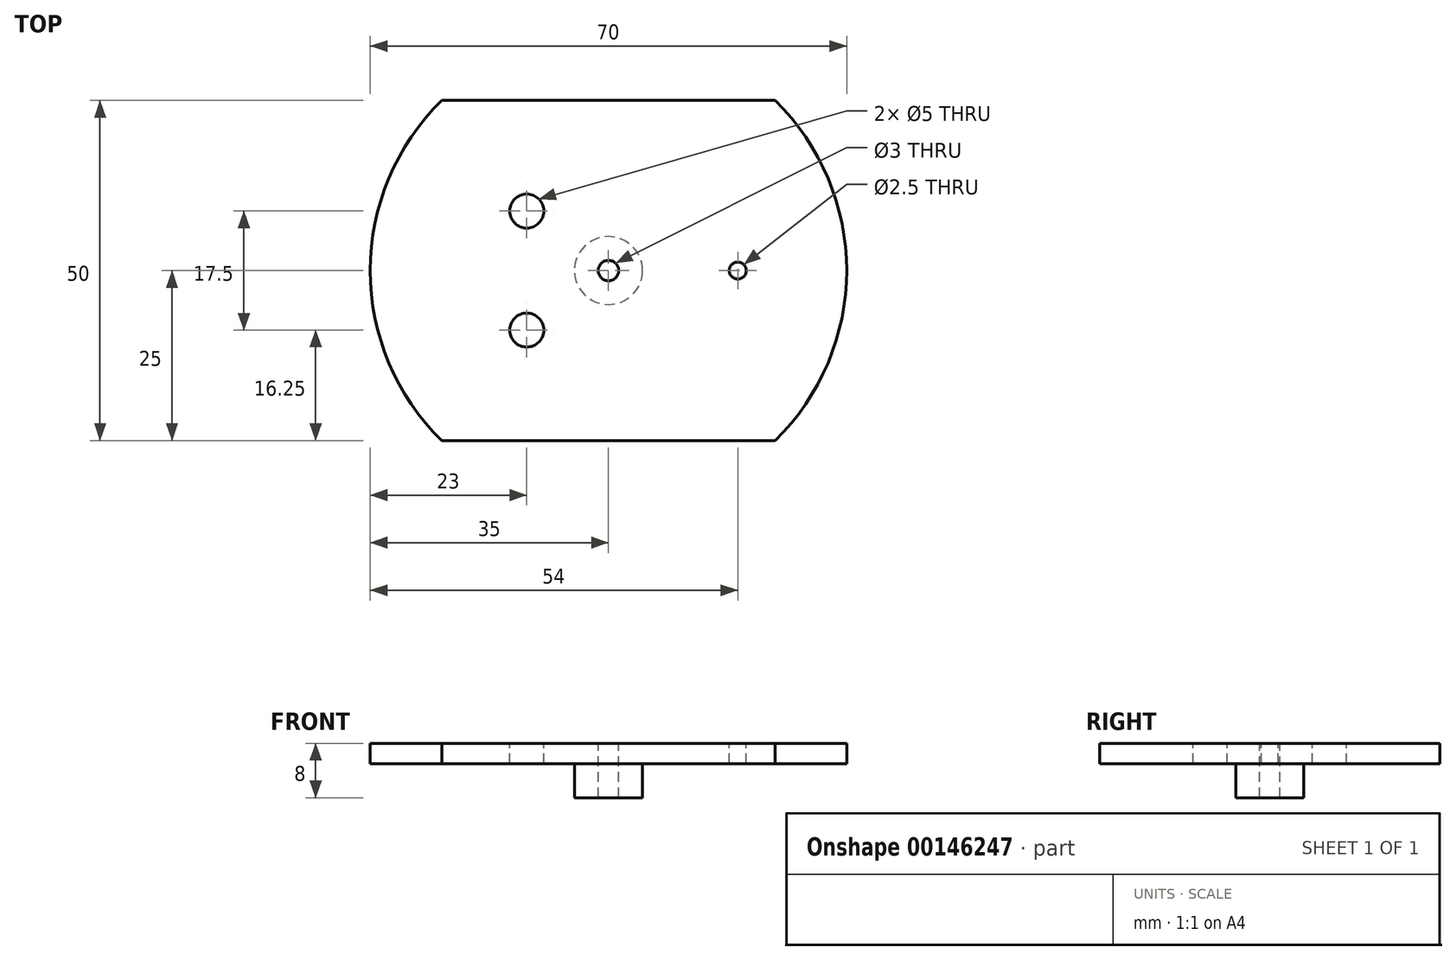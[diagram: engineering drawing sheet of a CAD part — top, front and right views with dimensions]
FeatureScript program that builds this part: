
annotation { "Feature Type Name" : "Feature", "Feature Type Description" : "" }
export const myFeature = defineFeature(function(context is Context, id is Id, definition is map)
    precondition{}
    {
        {
            var Q0;
            Q0=qCreatedBy(makeId("Top.planeOp"),FACE);
            var sketch = newSketch(context, id + "F0", { "sketchPlane" : qUnion([Q0])});
            skCircle(sketch, "E0", {"center": v(0, 0) * mm, "radius": 35 * mm});
            skSolve(sketch);
        }
        {
            var Q0;
            Q0=makeQuery(id+"F0.imprint","IMPRINT",FACE,{"disambiguationData":[TD([[makeQuery(id+"F0.imprint","IMPRINT",EDGE,{"derivedFrom":sQuery(id+"F0.wireOp",EDGE,"E0")}),1.0]])]});
            var Q1;
            Q1=makeQuery(id+"F0.imprint","IMPRINT",FACE,{"disambiguationData":[TD([[makeQuery(id+"F0.imprint","IMPRINT",EDGE,{"derivedFrom":sQuery(id+"F0.wireOp",EDGE,"Whwx3lis-mmVc-QAmH-rbGM-ZXvDKV8Y0eNu")}),1.0]])]});
            extrude(context, id + "F1", {"entities" : qUnion([Q0, Q1]), "depth" : 3 * mm});
        }
        {
            var Q0;
            Q0=makeQuery(id+"F1.opExtrude","CAP_FACE",FACE,{"disambiguationData":[OSD([sQuery(id+"F0.wireOp",EDGE,"E0")])],"isStart":true});
            var sketch = newSketch(context, id + "F2", { "sketchPlane" : qUnion([Q0])});
            skCircle(sketch, "E1", {"center": v(0, 0) * mm, "radius": 5 * mm});
            skSolve(sketch);
        }
        {
            var Q0;
            Q0 = qSketchRegion(id + "F2", true);
            extrude(context, id + "F3", {"entities" : qUnion([Q0]), "operationType" : NewBodyOperationType.ADD, "depth" : 5 * mm});
        }
        {
            var Q0;
            Q0=makeQuery(id+"F1.opExtrude","CAP_FACE",FACE,{"disambiguationData":[OSD([sQuery(id+"F0.wireOp",EDGE,"E0")])],"isStart":false});
            var sketch = newSketch(context, id + "F4", { "sketchPlane" : qUnion([Q0])});
            skCircle(sketch, "E2", {"center": v(0, 0) * mm, "radius": 1.5 * mm});
            skCircle(sketch, "E3", {"center": v(-12, 8.75) * mm, "radius": 2.5 * mm});
            skCircle(sketch, "E4", {"center": v(-12, -8.75) * mm, "radius": 2.5 * mm});
            skCircle(sketch, "E5", {"center": v(19, 0) * mm, "radius": 1.25 * mm});
            skSolve(sketch);
        }
        {
            var Q0;
            Q0=makeQuery(id+"F4.imprint","IMPRINT",FACE,{"disambiguationData":[TD([[makeQuery(id+"F4.imprint","IMPRINT",EDGE,{"derivedFrom":sQuery(id+"F4.wireOp",EDGE,"E2")}),1.0]])]});
            var Q1;
            Q1=makeQuery(id+"F4.imprint","IMPRINT",FACE,{"disambiguationData":[TD([[makeQuery(id+"F4.imprint","IMPRINT",EDGE,{"derivedFrom":sQuery(id+"F4.wireOp",EDGE,"E3")}),1.0]])]});
            var Q2;
            Q2=makeQuery(id+"F4.imprint","IMPRINT",FACE,{"disambiguationData":[TD([[makeQuery(id+"F4.imprint","IMPRINT",EDGE,{"derivedFrom":sQuery(id+"F4.wireOp",EDGE,"E4")}),1.0]])]});
            var Q3;
            Q3=makeQuery(id+"F4.imprint","IMPRINT",FACE,{"disambiguationData":[TD([[makeQuery(id+"F4.imprint","IMPRINT",EDGE,{"derivedFrom":sQuery(id+"F4.wireOp",EDGE,"E5")}),1.0]])]});
            extrude(context, id + "F5", {"entities" : qUnion([Q0, Q1, Q2, Q3]), "operationType" : NewBodyOperationType.REMOVE, "endBound" : BoundingType.THROUGH_ALL, "oppositeDirection" : true, "depth" : 25 * mm});
        }
        {
            var Q0;
            Q0=qCreatedBy(makeId("Top.planeOp"),FACE);
            var sketch = newSketch(context, id + "F6", { "sketchPlane" : qUnion([Q0])});
            skLineSegment(sketch, "E6.bottom", {"start": v(35, -25) * mm, "end": v(-35, -25) * mm});
            skLineSegment(sketch, "E6.top", {"start": v(35, 25) * mm, "end": v(-35, 25) * mm});
            skLineSegment(sketch, "E6.left", {"start": v(35, -25) * mm, "end": v(35, 25) * mm});
            skLineSegment(sketch, "E6.right", {"start": v(-35, -25) * mm, "end": v(-35, 25) * mm});
            skPoint(sketch, "E6.middle", {"position": v(0, 0) * mm});
            skSolve(sketch);
        }
        {
            var Q0;
            Q0=makeQuery(id+"F6.imprint","IMPRINT",FACE,{"disambiguationData":[TD([[makeQuery(id+"F6.imprint","IMPRINT",EDGE,{"derivedFrom":sQuery(id+"F6.wireOp",EDGE,"E6.bottom")}),-1.0]])]});
            extrude(context, id + "F7", {"entities" : qUnion([Q0]), "operationType" : NewBodyOperationType.INTERSECT, "endBound" : BoundingType.SYMMETRIC, "depth" : 20 * mm});
        }
    });
